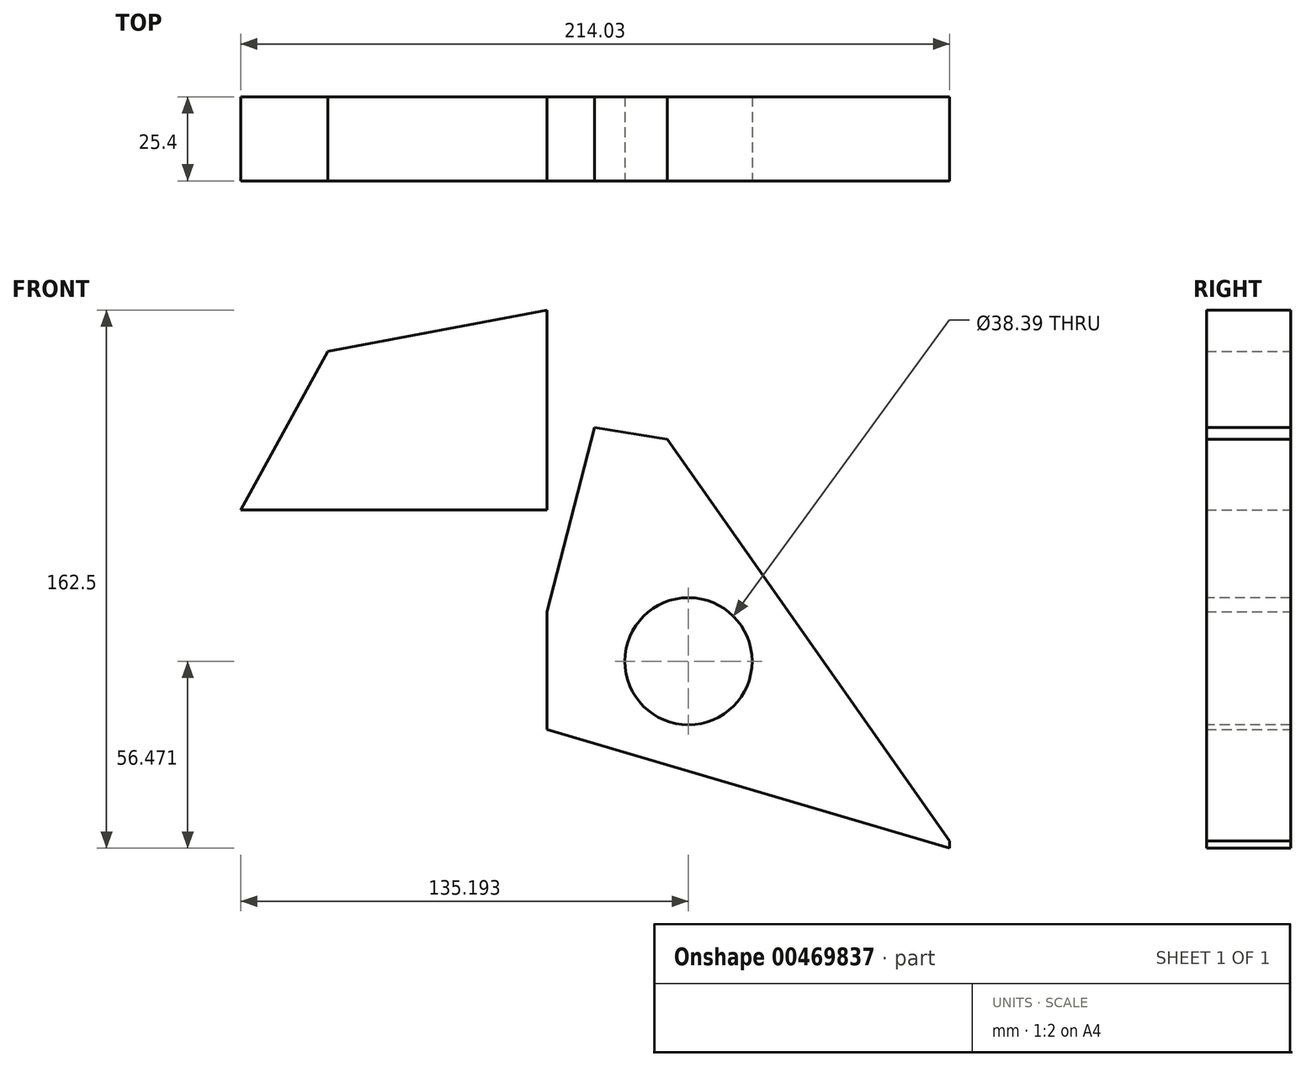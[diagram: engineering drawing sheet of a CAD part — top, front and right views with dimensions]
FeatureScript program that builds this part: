
annotation { "Feature Type Name" : "Feature", "Feature Type Description" : "" }
export const myFeature = defineFeature(function(context is Context, id is Id, definition is map)
    precondition{}
    {
        {
            var Q0;
            Q0=qCreatedBy(makeId("Front.planeOp"),FACE);
            var sketch = newSketch(context, id + "F0", { "sketchPlane" : qUnion([Q0])});
            skLineSegment(sketch, "E0", {"start": v(0, 6.57) * mm, "end": v(0, 0) * mm});
            skLineSegment(sketch, "E1", {"start": v(0, 0) * mm, "end": v(14.32, 55.56) * mm});
            skLineSegment(sketch, "E2", {"start": v(14.32, 55.56) * mm, "end": v(36.24, 52.02) * mm});
            skLineSegment(sketch, "E3", {"start": v(36.24, 52.02) * mm, "end": v(121.53, -69.23) * mm});
            skLineSegment(sketch, "E4", {"start": v(121.53, -69.23) * mm, "end": v(121.46, -71.46) * mm});
            skLineSegment(sketch, "E5", {"start": v(121.46, -71.46) * mm, "end": v(0, -35.6) * mm});
            skLineSegment(sketch, "E6", {"start": v(0, -35.6) * mm, "end": v(0, 27.78) * mm});
            skPoint(sketch, "E6.endSnap0", {"position": v(7.16, 27.78) * mm});
            skSolve(sketch);
        }
        {
            var Q0;
            {var subQ0=sQuery(id+"F0.wireOp",EDGE,"E1");Q0=makeQuery(id+"F0.imprint","IMPRINT",FACE,{"disambiguationData":[TD([[makeQuery(id+"F0.imprint","IMPRINT",EDGE,{"derivedFrom":subQ0}),-1.0]])]});}
            extrude(context, id + "F1", {"entities" : qUnion([Q0]), "depth" : 25.4 * mm});
        }
        {
            var Q0;
            Q0=makeQuery(id+"F1.opExtrude","CAP_FACE",FACE,{"disambiguationData":[OSD([sQuery(id+"F0.wireOp",EDGE,"E1"),sQuery(id+"F0.wireOp",EDGE,"E2"),sQuery(id+"F0.wireOp",EDGE,"E3"),sQuery(id+"F0.wireOp",EDGE,"E4"),sQuery(id+"F0.wireOp",EDGE,"E5"),sQuery(id+"F0.wireOp",EDGE,"E6")])],"isStart":false});
            var sketch = newSketch(context, id + "F2", { "sketchPlane" : qUnion([Q0])});
            skCircle(sketch, "E7", {"center": v(42.7, -14.99) * mm, "radius": 19.2 * mm});
            skSolve(sketch);
        }
        {
            var Q0;
            Q0=makeQuery(id+"F2.imprint","IMPRINT",FACE,{"disambiguationData":[TD([[makeQuery(id+"F2.imprint","IMPRINT",EDGE,{"derivedFrom":sQuery(id+"F2.wireOp",EDGE,"E7")}),1.0]])]});
            extrude(context, id + "F3", {"entities" : qUnion([Q0]), "operationType" : NewBodyOperationType.REMOVE, "oppositeDirection" : true, "depth" : 25.4 * mm});
        }
        {
            var Q0;
            Q0=qCreatedBy(makeId("Front.planeOp"),FACE);
            var sketch = newSketch(context, id + "F4", { "sketchPlane" : qUnion([Q0])});
            skLineSegment(sketch, "E8", {"start": v(-95.95, 24.33) * mm, "end": v(-66.23, 78.59) * mm});
            skLineSegment(sketch, "E9", {"start": v(-66.23, 78.59) * mm, "end": v(0, 91.04) * mm});
            skLineSegment(sketch, "E10", {"start": v(0, 91.04) * mm, "end": v(0, 30.64) * mm});
            skLineSegment(sketch, "E11", {"start": v(0, 30.64) * mm, "end": v(-104.56, 30.64) * mm});
            skSolve(sketch);
        }
        {
            var Q0;
            {var subQ0=sQuery(id+"F4.wireOp",EDGE,"E9");Q0=makeQuery(id+"F4.imprint","IMPRINT",FACE,{"disambiguationData":[TD([[makeQuery(id+"F4.imprint","IMPRINT",EDGE,{"derivedFrom":subQ0}),-1.0]])]});}
            extrude(context, id + "F5", {"entities" : qUnion([Q0]), "depth" : 25.4 * mm});
        }
    });
